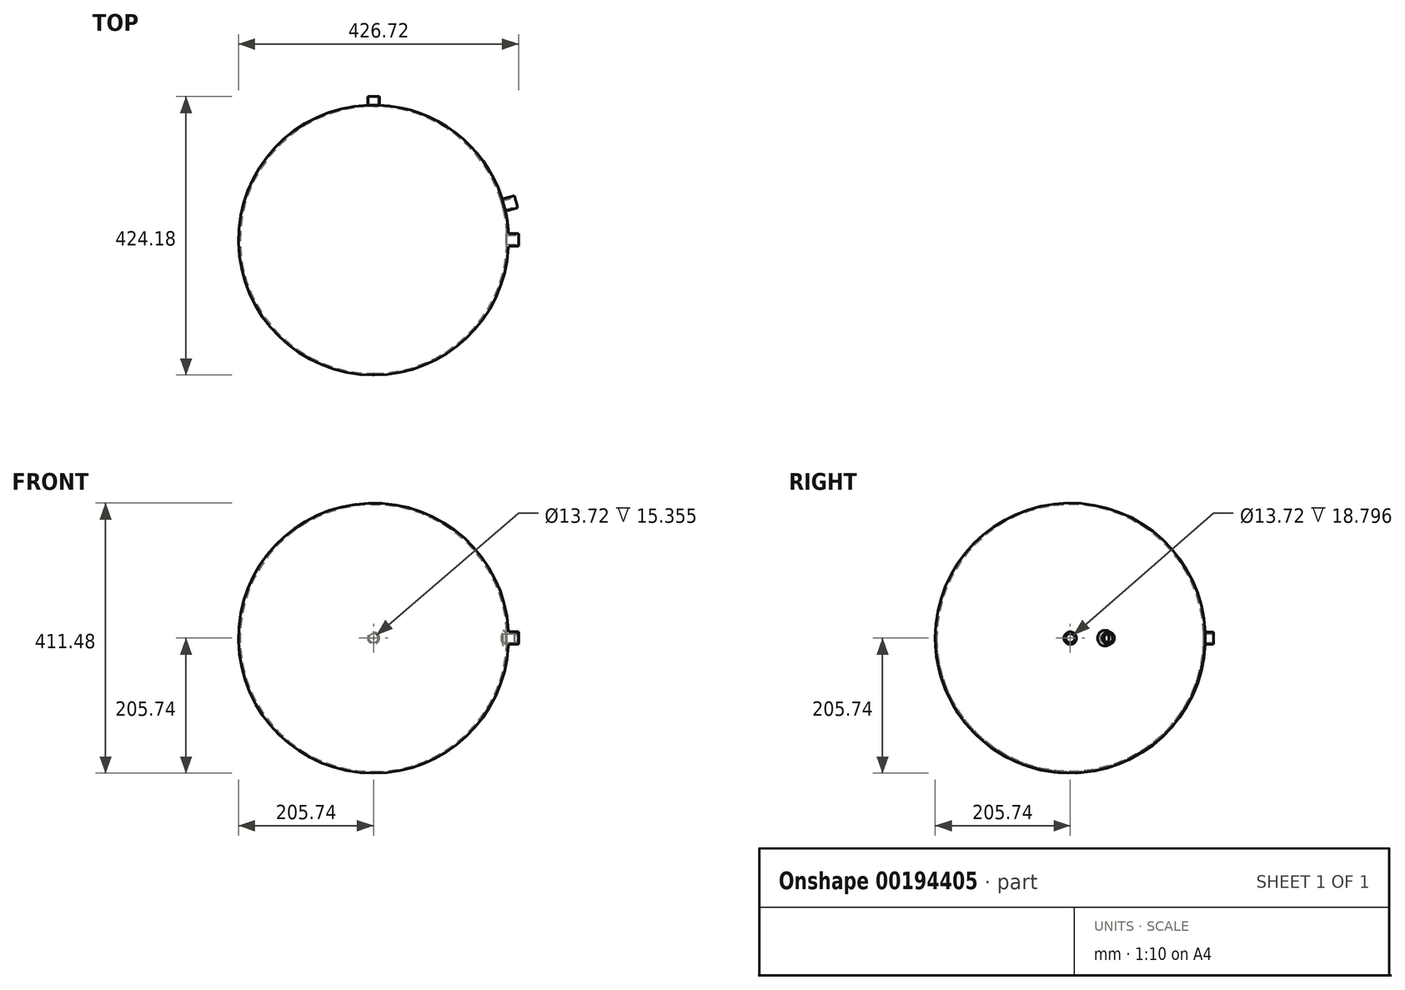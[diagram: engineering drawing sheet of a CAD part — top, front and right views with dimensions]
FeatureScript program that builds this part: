
annotation { "Feature Type Name" : "Feature", "Feature Type Description" : "" }
export const myFeature = defineFeature(function(context is Context, id is Id, definition is map)
    precondition{}
    {
        {
            var Q0;
            Q0=qCreatedBy(makeId("Top.planeOp"),FACE);
            var sketch = newSketch(context, id + "F0", { "sketchPlane" : qUnion([Q0])});
            skLineSegment(sketch, "E0", {"start": v(0, 0) * mm, "end": v(203.2, 0) * mm});
            skArc(sketch, "E1", {"start": v(0.55, -203.2) * mm, "mid": v(203.2, 0.27) * mm, "end": v(0, 203.2) * mm});
            skArc(sketch, "E2.0", {"start": v(0.55, -205.74) * mm, "mid": v(139.2, -151.5) * mm, "end": v(204.96, -17.94) * mm});
            skLineSegment(sketch, "E3", {"start": v(0.55, -205.74) * mm, "end": v(0.55, -203.2) * mm});
            skLineSegment(sketch, "E4", {"start": v(0, 0) * mm, "end": v(0, 127) * mm});
            skArc(sketch, "E5.trimOffspring", {"start": v(204.96, 17.94) * mm, "mid": v(142.27, 148.62) * mm, "end": v(8.97, 205.54) * mm});
            skLineSegment(sketch, "E6", {"start": v(0, 218.44) * mm, "end": v(8.97, 218.44) * mm});
            skLineSegment(sketch, "E7", {"start": v(8.97, 218.44) * mm, "end": v(8.97, 205.54) * mm});
            skLineSegment(sketch, "E8.trimOffspring", {"start": v(0, 203.2) * mm, "end": v(0, 218.44) * mm});
            skArc(sketch, "E9", {"start": v(0.55, -205.74) * mm, "mid": v(205.74, 0.28) * mm, "end": v(0, 205.74) * mm});
            skLineSegment(sketch, "E10", {"start": v(0, 0) * mm, "end": v(198.73, 53.25) * mm});
            skSolve(sketch);
        }
        {
            var Q0;
            {var subQ0=sQuery(id+"F0.wireOp",EDGE,"E6");Q0=makeQuery(id+"F0.imprint","IMPRINT",FACE,{"disambiguationData":[TD([[makeQuery(id+"F0.imprint","IMPRINT",EDGE,{"derivedFrom":subQ0}),-1.0]])]});}
            var Q1;
            {var subQ5=sQuery(id+"F0.wireOp",EDGE,"E3");Q1=makeQuery(id+"F0.imprint","IMPRINT",FACE,{"disambiguationData":[TD([[makeQuery(id+"F0.imprint","IMPRINT",EDGE,{"derivedFrom":subQ5}),-1.0]])]});}
            var Q2;
            {var subQ2=sQuery(id+"F0.wireOp",EDGE,"E8.trimOffspring");var subQ6=sQuery(id+"F0.wireOp",EDGE,"E1");var subQ7=makeQuery(id+"F0.imprint","INTERSECT",VERTEX,{"derivedFrom":[subQ6,subQ2]});Q2=makeQuery(id+"F0.imprint","IMPRINT",FACE,{"disambiguationData":[TD([[makeQuery(id+"F0.imprint","IMPRINT",EDGE,{"disambiguationData":[TD([[subQ7,1.0]])],"derivedFrom":subQ6}),-1.0]])]});}
            var Q3;
            Q3=sQuery(id+"F0.wireOp",EDGE,"E4");
            revolve(context, id + "F1", {"entities" : qUnion([Q0, Q1, Q2]), "axis" : qUnion([Q3]), "revolveType" : RevolveType.FULL});
        }
        {
            var Q0;
            Q0=makeQuery(id+"F1.opRevolve","SWEPT_FACE",FACE,{"disambiguationData":[OSD([sQuery(id+"F0.wireOp",EDGE,"E6")])]});
            var sketch = newSketch(context, id + "F2", { "sketchPlane" : qUnion([Q0])});
            skCircle(sketch, "E11", {"center": v(0, 0) * mm, "radius": 6.86 * mm});
            skSolve(sketch);
        }
        {
            var Q0;
            Q0=makeQuery(id+"F2.imprint","IMPRINT",FACE,{"disambiguationData":[TD([[makeQuery(id+"F2.imprint","IMPRINT",EDGE,{"derivedFrom":sQuery(id+"F2.wireOp",EDGE,"E11")}),1.0]])]});
            extrude(context, id + "F3", {"entities" : qUnion([Q0]), "operationType" : NewBodyOperationType.REMOVE, "oppositeDirection" : true, "depth" : 25.4 * mm});
        }
        {
            var Q0;
            Q0=sQuery(id+"F0.wireOp",EDGE,"E0");
            cPlane(context, id + "F4", {"entities" : qUnion([Q0]), "cplaneType" : CPlaneType.LINE_ANGLE, "offset" : 25.4 * mm, "angle" : 0 * degree, "width" : 152.4 * mm, "height" : 152.4 * mm});
        }
        {
            var Q0;
            Q0=qCreatedBy(id+"F4.planeOp",FACE);
            var sketch = newSketch(context, id + "F5", { "sketchPlane" : qUnion([Q0])});
            skLineSegment(sketch, "E12", {"start": v(-205.74, 0) * mm, "end": v(-205.74, 154.5) * mm});
            skSolve(sketch);
        }
        {
            var Q0;
            Q0=sQuery(id+"F5.wireOp",EDGE,"E12");
            cPlane(context, id + "F6", {"entities" : qUnion([Q0]), "cplaneType" : CPlaneType.LINE_ANGLE, "offset" : 25.4 * mm, "angle" : 0 * degree, "width" : 152.4 * mm, "height" : 152.4 * mm});
        }
        {
            var Q0;
            Q0=qCreatedBy(id+"F6.planeOp",FACE);
            var sketch = newSketch(context, id + "F7", { "sketchPlane" : qUnion([Q0])});
            skCircle(sketch, "E13", {"center": v(0, 0) * mm, "radius": 9.53 * mm});
            skSolve(sketch);
        }
        {
            var Q0;
            Q0=makeQuery(id+"F7.imprint","IMPRINT",FACE,{"disambiguationData":[TD([[makeQuery(id+"F7.imprint","IMPRINT",EDGE,{"derivedFrom":sQuery(id+"F7.wireOp",EDGE,"E13")}),1.0]])]});
            extrude(context, id + "F8", {"entities" : qUnion([Q0]), "operationType" : NewBodyOperationType.ADD, "depth" : 15.24 * mm, "hasSecondDirection" : true, "secondDirectionOppositeDirection" : true, "secondDirectionDepth" : 3.56 * mm});
        }
        {
            var Q0;
            Q0=makeQuery(id+"F8.boolean.opBoolean","INTERSECT",EDGE,{"derivedFrom":[makeQuery(id+"F1.opRevolve","SWEPT_FACE",FACE,{"disambiguationData":[OSD([sQuery(id+"F0.wireOp",EDGE,"E9")])]}),makeQuery(id+"F8.opExtrude","SWEPT_FACE",FACE,{"disambiguationData":[OSD([sQuery(id+"F7.wireOp",EDGE,"E13")])]})]});
            fillet(context, id + "F9", {"entities" : qUnion([Q0]), "radius" : 2.54 * mm, "tangentPropagation" : true, "allowEdgeOverflow" : false});
        }
        {
            var Q0;
            Q0=sQuery(id+"F0.wireOp",EDGE,"E10");
            cPlane(context, id + "F10", {"entities" : qUnion([Q0]), "cplaneType" : CPlaneType.LINE_ANGLE, "offset" : 25.4 * mm, "angle" : 0 * degree, "width" : 152.4 * mm, "height" : 152.4 * mm});
        }
        {
            var Q0;
            Q0=qCreatedBy(id+"F10.planeOp",FACE);
            var sketch = newSketch(context, id + "F11", { "sketchPlane" : qUnion([Q0])});
            skLineSegment(sketch, "E14", {"start": v(-205.74, 0) * mm, "end": v(-205.74, 788.82) * mm});
            skSolve(sketch);
        }
        {
            var Q0;
            Q0=sQuery(id+"F11.wireOp",EDGE,"E14");
            cPlane(context, id + "F12", {"entities" : qUnion([Q0]), "cplaneType" : CPlaneType.LINE_ANGLE, "offset" : 25.4 * mm, "angle" : 15 * degree, "width" : 152.4 * mm, "height" : 152.4 * mm});
        }
        {
            var Q0;
            Q0=qCreatedBy(id+"F12.planeOp",FACE);
            var sketch = newSketch(context, id + "F13", { "sketchPlane" : qUnion([Q0])});
            skCircle(sketch, "E15", {"center": v(0, 0) * mm, "radius": 9.53 * mm});
            skSolve(sketch);
        }
        {
            var Q0;
            Q0=makeQuery(id+"F13.imprint","IMPRINT",FACE,{"disambiguationData":[TD([[makeQuery(id+"F13.imprint","IMPRINT",EDGE,{"derivedFrom":sQuery(id+"F13.wireOp",EDGE,"E15")}),1.0]])]});
            extrude(context, id + "F14", {"entities" : qUnion([Q0]), "operationType" : NewBodyOperationType.ADD, "depth" : 19.05 * mm, "hasSecondDirection" : true, "secondDirectionOppositeDirection" : true, "secondDirectionDepth" : 2.54 * mm});
        }
        {
            var Q0;
            Q0=makeQuery(id+"F14.boolean.opBoolean","INTERSECT",EDGE,{"derivedFrom":[makeQuery(id+"F1.opRevolve","SWEPT_FACE",FACE,{"disambiguationData":[OSD([sQuery(id+"F0.wireOp",EDGE,"E9")])]}),makeQuery(id+"F14.opExtrude","SWEPT_FACE",FACE,{"disambiguationData":[OSD([sQuery(id+"F13.wireOp",EDGE,"E15")])]})]});
            fillet(context, id + "F15", {"entities" : qUnion([Q0]), "radius" : 2.54 * mm, "tangentPropagation" : true, "allowEdgeOverflow" : false});
        }
        {
            var Q0;
            Q0=makeQuery(id+"F8.opExtrude","CAP_FACE",FACE,{"disambiguationData":[OSD([sQuery(id+"F7.wireOp",EDGE,"E13")])],"isStart":false});
            var sketch = newSketch(context, id + "F16", { "sketchPlane" : qUnion([Q0])});
            skCircle(sketch, "E16", {"center": v(0, 0) * mm, "radius": 6.86 * mm});
            skSolve(sketch);
        }
        {
            var Q0;
            Q0=makeQuery(id+"F14.opExtrude","CAP_FACE",FACE,{"disambiguationData":[OSD([sQuery(id+"F13.wireOp",EDGE,"E15")])],"isStart":false});
            var sketch = newSketch(context, id + "F17", { "sketchPlane" : qUnion([Q0])});
            skCircle(sketch, "E17", {"center": v(0, 0) * mm, "radius": 6.86 * mm});
            skSolve(sketch);
        }
        {
            var Q0;
            Q0=makeQuery(id+"F17.imprint","IMPRINT",FACE,{"disambiguationData":[TD([[makeQuery(id+"F17.imprint","IMPRINT",EDGE,{"derivedFrom":sQuery(id+"F17.wireOp",EDGE,"E17")}),1.0]])]});
            extrude(context, id + "F18", {"entities" : qUnion([Q0]), "operationType" : NewBodyOperationType.REMOVE, "oppositeDirection" : true, "depth" : 25.4 * mm});
        }
        {
            var Q0;
            Q0=makeQuery(id+"F16.imprint","IMPRINT",FACE,{"disambiguationData":[TD([[makeQuery(id+"F16.imprint","IMPRINT",EDGE,{"derivedFrom":sQuery(id+"F16.wireOp",EDGE,"E16")}),1.0]])]});
            extrude(context, id + "F19", {"entities" : qUnion([Q0]), "operationType" : NewBodyOperationType.REMOVE, "oppositeDirection" : true, "depth" : 25.4 * mm});
        }
    });
